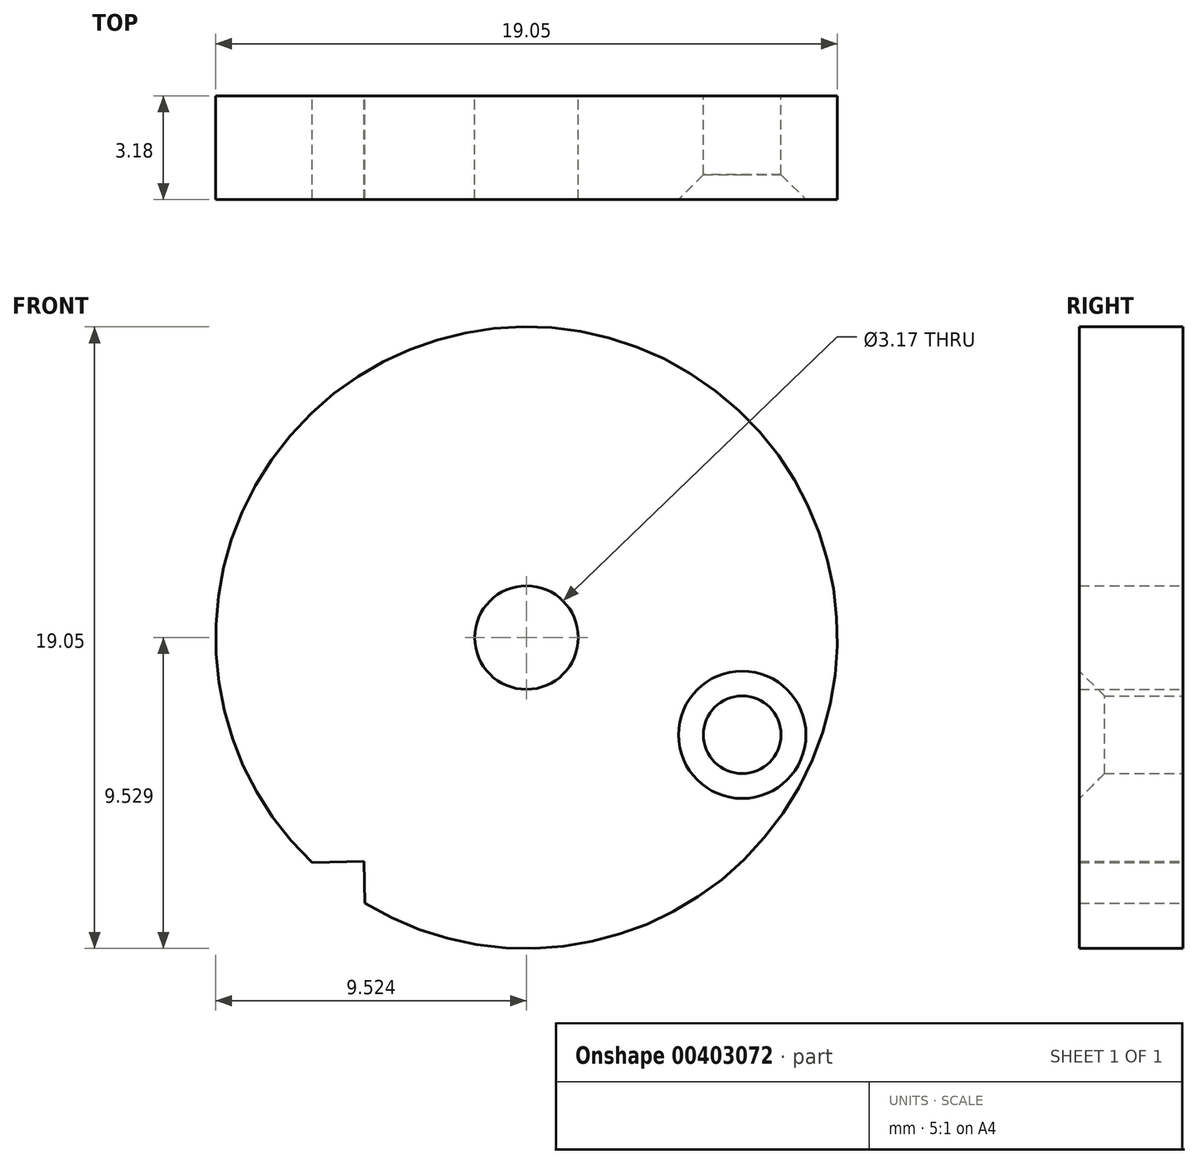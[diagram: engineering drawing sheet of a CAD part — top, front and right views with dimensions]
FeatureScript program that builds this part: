
annotation { "Feature Type Name" : "Feature", "Feature Type Description" : "" }
export const myFeature = defineFeature(function(context is Context, id is Id, definition is map)
    precondition{}
    {
        {
            var Q0;
            Q0=qCreatedBy(makeId("Front.planeOp"),FACE);
            var sketch = newSketch(context, id + "F0", { "sketchPlane" : qUnion([Q0])});
            skArc(sketch, "E0", {"start": v(-4.16, -4.72) * mm, "mid": v(6.58, 10.98) * mm, "end": v(-5.78, -3.48) * mm});
            skCircle(sketch, "E1", {"center": v(0.78, 3.42) * mm, "radius": 1.59 * mm});
            skLineSegment(sketch, "E2", {"start": v(-5.78, -3.48) * mm, "end": v(-4.2, -3.44) * mm});
            skLineSegment(sketch, "E3", {"start": v(-4.2, -3.44) * mm, "end": v(-4.16, -4.72) * mm});
            skCircle(sketch, "E4", {"center": v(7.4, 0.44) * mm, "radius": 1.2 * mm});
            skSolve(sketch);
        }
        {
            var Q0;
            Q0=makeQuery(id+"F0.imprint","IMPRINT",FACE,{"disambiguationData":[TD([[makeQuery(id+"F0.imprint","IMPRINT",EDGE,{"derivedFrom":sQuery(id+"F0.wireOp",EDGE,"E0")}),1.0]])]});
            extrude(context, id + "F1", {"entities" : qUnion([Q0]), "endBound" : BoundingType.SYMMETRIC, "depth" : 3.17 * mm});
        }
        {
            var Q0;
            Q0=makeQuery(id+"F1.opExtrude","CAP_EDGE",EDGE,{"disambiguationData":[OSD([sQuery(id+"F0.wireOp",EDGE,"E4")])],"isStart":false});
            chamfer(context, id + "F2", {"entities" : qUnion([Q0]), "width" : 0.76 * mm, "tangentPropagation" : true});
        }
    });
